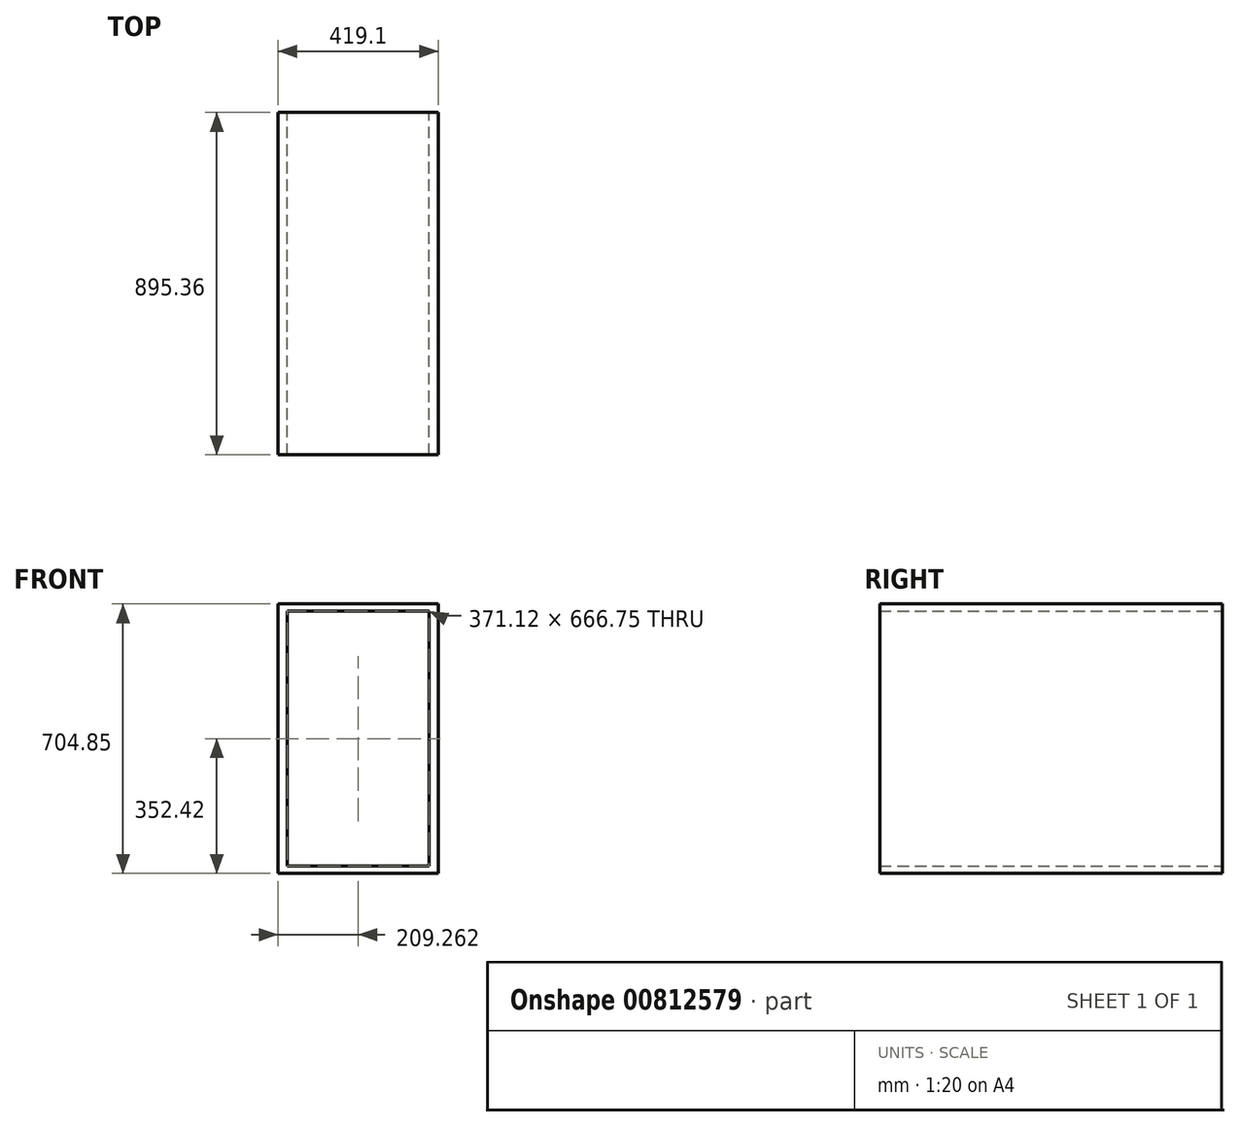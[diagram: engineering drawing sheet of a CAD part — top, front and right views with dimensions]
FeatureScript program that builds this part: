
annotation { "Feature Type Name" : "Feature", "Feature Type Description" : "" }
export const myFeature = defineFeature(function(context is Context, id is Id, definition is map)
    precondition{}
    {
        {
            var Q0;
            Q0=qCreatedBy(makeId("Front.planeOp"),FACE);
            var sketch = newSketch(context, id + "F0", { "sketchPlane" : qUnion([Q0])});
            skLineSegment(sketch, "E0.bottom", {"start": v(209.55, 9.52) * mm, "end": v(-209.55, 9.52) * mm});
            skLineSegment(sketch, "E0.top", {"start": v(209.55, -9.53) * mm, "end": v(-209.55, -9.53) * mm});
            skLineSegment(sketch, "E0.left", {"start": v(209.55, 9.52) * mm, "end": v(209.55, -9.53) * mm});
            skLineSegment(sketch, "E0.right", {"start": v(-209.55, 9.53) * mm, "end": v(-209.55, -9.53) * mm});
            skPoint(sketch, "E0.middle", {"position": v(0, 0) * mm});
            skLineSegment(sketch, "E1.bottom", {"start": v(-209.55, -9.53) * mm, "end": v(-185.85, -9.53) * mm});
            skLineSegment(sketch, "E1.top", {"start": v(-209.55, -676.28) * mm, "end": v(-185.85, -676.28) * mm});
            skLineSegment(sketch, "E1.left", {"start": v(-209.55, -9.53) * mm, "end": v(-209.55, -676.28) * mm});
            skLineSegment(sketch, "E1.right", {"start": v(-185.85, -9.53) * mm, "end": v(-185.85, -676.28) * mm});
            skLineSegment(sketch, "E2.bottom", {"start": v(209.55, -9.53) * mm, "end": v(185.27, -9.53) * mm});
            skLineSegment(sketch, "E2.top", {"start": v(209.55, -676.28) * mm, "end": v(185.27, -676.28) * mm});
            skLineSegment(sketch, "E2.left", {"start": v(209.55, -9.53) * mm, "end": v(209.55, -676.27) * mm});
            skLineSegment(sketch, "E2.right", {"start": v(185.27, -9.53) * mm, "end": v(185.27, -676.28) * mm});
            skLineSegment(sketch, "E3.bottom", {"start": v(-209.55, -676.28) * mm, "end": v(209.55, -676.28) * mm});
            skLineSegment(sketch, "E3.top", {"start": v(-209.55, -695.32) * mm, "end": v(209.55, -695.32) * mm});
            skLineSegment(sketch, "E3.left", {"start": v(-209.55, -676.28) * mm, "end": v(-209.55, -695.32) * mm});
            skLineSegment(sketch, "E3.right", {"start": v(209.55, -676.27) * mm, "end": v(209.55, -695.32) * mm});
            skLineSegment(sketch, "E4.bottom", {"start": v(-185.85, -9.53) * mm, "end": v(185.27, -9.53) * mm});
            skLineSegment(sketch, "E4.top", {"start": v(-185.85, -644.52) * mm, "end": v(185.27, -644.52) * mm});
            skLineSegment(sketch, "E4.left", {"start": v(-185.85, -9.53) * mm, "end": v(-185.85, -644.52) * mm});
            skLineSegment(sketch, "E4.right", {"start": v(185.27, -9.53) * mm, "end": v(185.27, -644.52) * mm});
            skSolve(sketch);
        }
        {
            var Q0;
            Q0 = qSketchRegion(id + "F0", true);
            extrude(context, id + "F1", {"entities" : qUnion([Q0]), "endBound" : BoundingType.SYMMETRIC, "depth" : 895.35 * mm, "hasOffset" : true, "offsetDistance" : 895.35 * mm});
        }
    });
